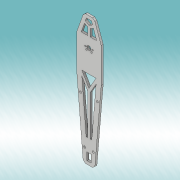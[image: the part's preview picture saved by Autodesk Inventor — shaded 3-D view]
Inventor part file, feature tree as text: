
AUTODESK INVENTOR PART (.ipt)
format: ipt  version: 2019 (Build 230136000, 136)  size: 206,336 bytes
history: native  units: mm
features: extrude x1
ambient origin geometry x8: Origin, YZ Plane, XZ Plane, XY Plane, X Axis, Y Axis, Z Axis, Center Point
bodies: Solid1 (feature_tree)
feature tree (1):
  extrude  "Extrusion1"  Depth=7.0mm
